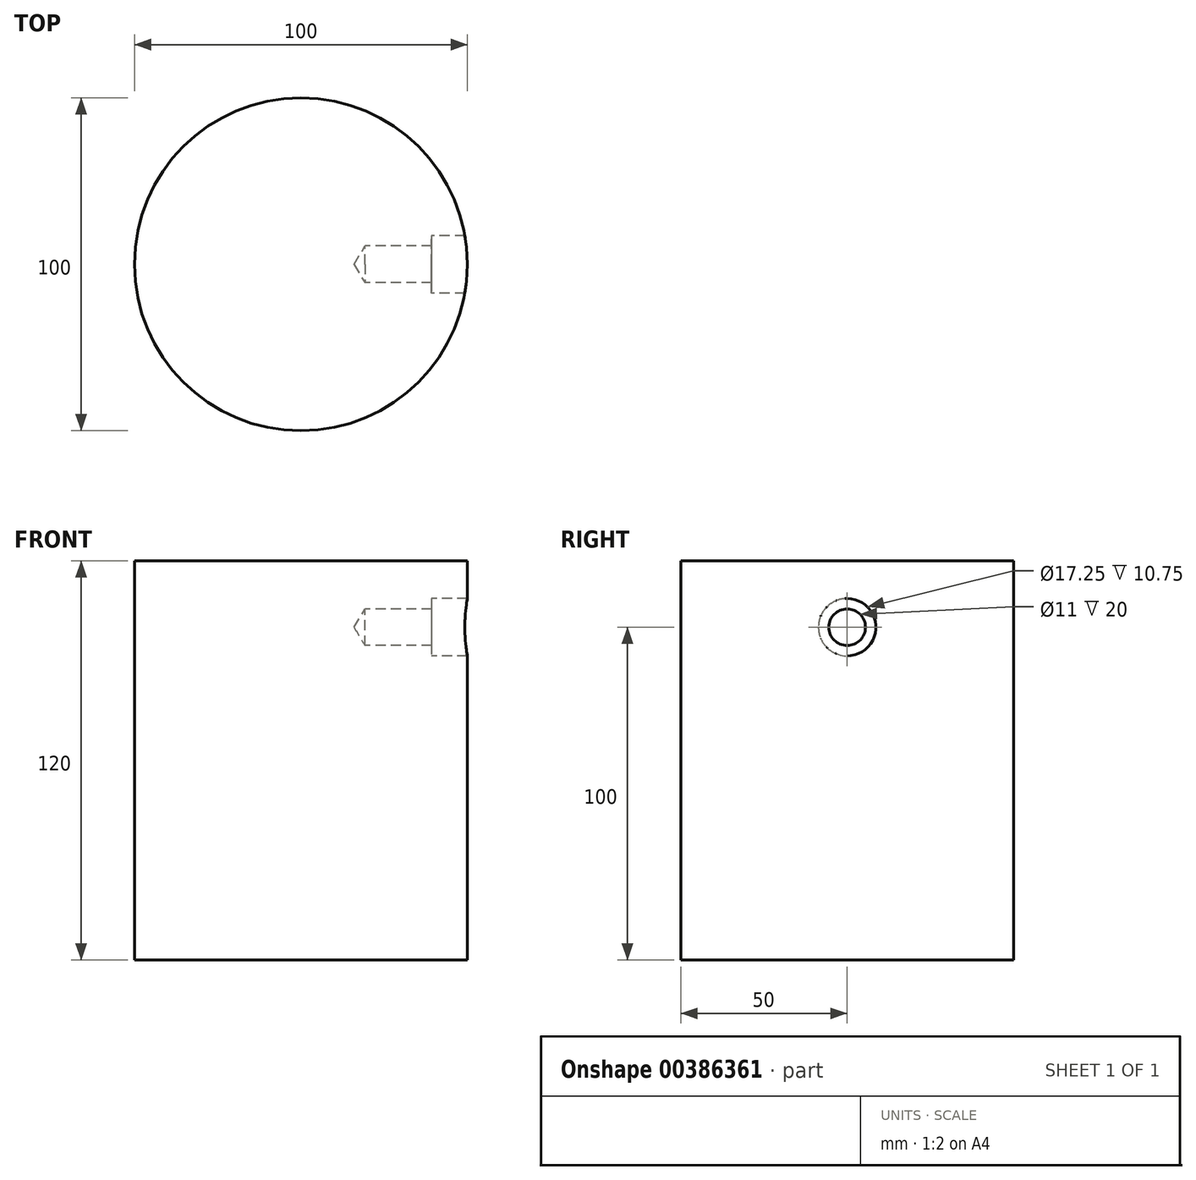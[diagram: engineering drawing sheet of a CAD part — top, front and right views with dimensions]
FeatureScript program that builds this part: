
annotation { "Feature Type Name" : "Feature", "Feature Type Description" : "" }
export const myFeature = defineFeature(function(context is Context, id is Id, definition is map)
    precondition{}
    {
        {
            var Q0;
            Q0=qCreatedBy(makeId("Top.planeOp"),FACE);
            var sketch = newSketch(context, id + "F0", { "sketchPlane" : qUnion([Q0])});
            skCircle(sketch, "E0", {"center": v(0, 0) * mm, "radius": 50 * mm});
            skPoint(sketch, "E1", {"position": v(50, 0) * mm});
            skSolve(sketch);
        }
        {
            var Q0;
            Q0=qSketchRegion(id+"F0",true);
            extrude(context, id + "F1", {"entities" : qUnion([Q0]), "depth" : 120 * mm});
        }
        {
            var Q0;
            Q0=sQuery(id+"F0.wireOp",VERTEX,"E1");
            var Q1;
            Q1=qCreatedBy(makeId("Right.planeOp"),FACE);
            cPlane(context, id + "F2", {"entities" : qUnion([Q0, Q1]), "cplaneType" : CPlaneType.PLANE_POINT, "offset" : 150 * mm, "width" : 150 * mm, "height" : 150 * mm});
        }
        {
            assignVariable(context, id + "F3", {"name" : "Height", "anyValue" : 100});
        }
        {
            var Q0;
            Q0=qCreatedBy(id+"F2.planeOp",FACE);
            var sketch = newSketch(context, id + "F4", { "sketchPlane" : qUnion([Q0])});
            skPoint(sketch, "E2", {"position": v(0, 100) * mm});
            skPoint(sketch, "E3", {"position": v(0, 0) * mm});
            skSolve(sketch);
        }
        {
            var Q0;
            Q0=sQuery(id+"F4.wireOp",VERTEX,"E2");
            var Q1;
            Q1=makeQuery(id+"F1.opExtrude","SWEPT_BODY",BODY,{"disambiguationData":[OSD([sQuery(id+"F0.wireOp",EDGE,"E0")])]});
            hole(context, id + "F5", {"style" : HoleStyle.C_BORE, "endStyle" : HoleEndStyle.BLIND, "standardTappedOrClearance" : lookupTablePath({ "standard" : "ISO", "fit" : "Normal", "size" : "M10", "type" : "Clearance" }), "standardBlindInLast" : lookupTablePath({ "fit" : "Standard", "standard" : "ISO", "size" : "M10", "type" : "Clearance" }), "holeDiameter" : 11 * mm, "cBoreDiameter" : 17.25 * mm, "cBoreDepth" : 10 * mm, "holeDepth" : 30 * mm, "locations" : qUnion([Q0]), "scope" : qUnion([Q1]), "startStyle" : HoleStartStyle.PART});
        }
        {
            assignVariable(context, id + "F6", {"name" : "Height", "anyValue" : getVariable(context, 'Height') - 5});
        }
    });
